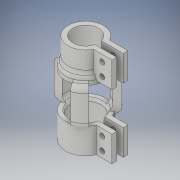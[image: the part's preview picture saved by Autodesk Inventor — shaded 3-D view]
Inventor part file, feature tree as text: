
AUTODESK INVENTOR PART (.ipt)
format: ipt  version: 2018 (Build 220112000, 112)  size: 410,624 bytes
history: native  units: in
note: dims shown in document units (in); Inventor stores cm internally (conversion verified against a paired STEP export)
features: fillet x6, extrude x5, sketch x5, projected_geometry x1
ambient origin geometry x8: Origin, YZ Plane, XZ Plane, XY Plane, X Axis, Y Axis, Z Axis, Center Point
bodies: Solid1 (feature_tree)
feature tree (17):
  extrude  "Extrusion1"  Depth=0.1875in
  extrude  "Extrusion2"  Depth=0.75in
  extrude  "Extrusion3"  Depth=0.1875in
  extrude  "Extrusion4"  Depth=0.25in
  fillet  "Fillet1"  Radius=1.5in
  fillet  "Fillet3"  [1 undecoded]
  fillet  "Fillet4"  [1 undecoded]
  fillet  "Fillet5"  [1 undecoded]
  fillet  "Fillet6"  Radius=0.6528in
  fillet  "Fillet7"  Radius=0.6528in
  extrude  "Extrusion5"  Depth=0.1875in
  sketch  "Sketch1"  dims[d18=1.19in d19=0.1875in]
  sketch  "Sketch2"  dims[d20=0.1875in d21=0.75in]
  sketch  "Sketch3"  dims[d22=0.25in d23=0.1875in]
  sketch  "Sketch4"  dims[d24=1.0in d25=0.0in d26=0.25in d27=1.5in d28=30.0deg d29=30.0deg d30=30.0deg d31=0.6528in d32=0.6528in]
  projected_geometry  "Projected Loop1"
  sketch  "Sketch5"  dims[d33=1.5in d34=0.0in d35=0.1875in d36=0.1875in d37=0.5in d38=0.25in d39=1.0in d40=0.0in d41=0.25in d42=0.0in d43=0.25in d45=0.25in d46=0.25in d47=0.25in d48=0.25in d49=0.25in d50=0.375in d51=0.375in d52=0.25in d53=0.25in d54=0.25in d55=0.25in d56=0.375in d57=0.375in d58=0.1935in d59=0.75in d60=0.0in]
note: 3 required parameter values undecoded (feature->parameter linkage not recoverable at this tier; creation-order binding heuristic only, values carry confidence <= 0.55)
